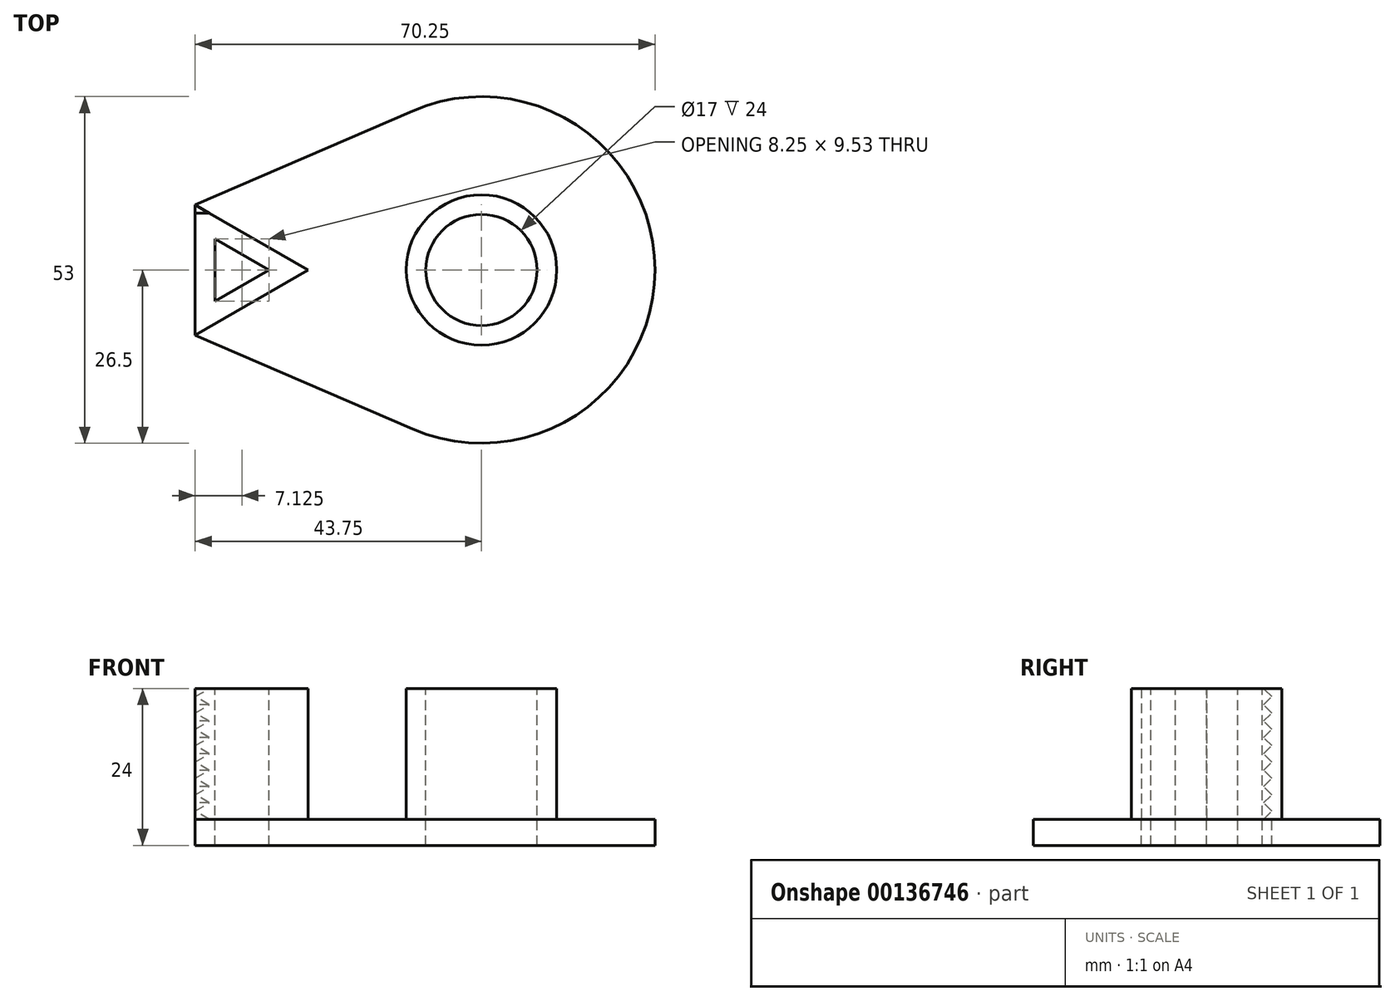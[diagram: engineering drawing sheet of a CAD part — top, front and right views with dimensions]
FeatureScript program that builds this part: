
annotation { "Feature Type Name" : "Feature", "Feature Type Description" : "" }
export const myFeature = defineFeature(function(context is Context, id is Id, definition is map)
    precondition{}
    {
        {
            var Q0;
            Q0=qCreatedBy(makeId("Top.planeOp"),FACE);
            var sketch = newSketch(context, id + "F0", { "sketchPlane" : qUnion([Q0])});
            skCircle(sketch, "E0", {"center": v(0, 0) * mm, "radius": 11.5 * mm});
            skCircle(sketch, "E1.cCircle", {"center": v(-38, 0) * mm, "radius": 11.5 * mm, "construction": true});
            skLineSegment(sketch, "E1.0", {"start": v(-26.5, 0) * mm, "end": v(-43.75, -9.96) * mm});
            skLineSegment(sketch, "E1.1", {"start": v(-43.75, -9.96) * mm, "end": v(-43.75, 9.96) * mm});
            skLineSegment(sketch, "E1.2", {"start": v(-43.75, 9.96) * mm, "end": v(-26.5, 0) * mm});
            skCircle(sketch, "E2", {"center": v(0, 0) * mm, "radius": 26.5 * mm});
            skCircle(sketch, "E3.0", {"center": v(0, 0) * mm, "radius": 8.5 * mm});
            skLineSegment(sketch, "E4.0", {"start": v(-40.75, -4.76) * mm, "end": v(-40.75, 4.76) * mm});
            skLineSegment(sketch, "E4.1", {"start": v(-32.5, 0) * mm, "end": v(-40.75, -4.76) * mm});
            skLineSegment(sketch, "E4.2", {"start": v(-40.75, 4.76) * mm, "end": v(-32.5, 0) * mm});
            skLineSegment(sketch, "E5", {"start": v(-43.75, 9.96) * mm, "end": v(-10.51, 24.32) * mm});
            skLineSegment(sketch, "E6", {"start": v(-43.75, -9.96) * mm, "end": v(-10.51, -24.32) * mm});
            skSolve(sketch);
        }
        {
            var Q0;
            Q0=makeQuery(id+"F0.imprint","IMPRINT",FACE,{"disambiguationData":[TD([[makeQuery(id+"F0.imprint","IMPRINT",EDGE,{"derivedFrom":sQuery(id+"F0.wireOp",EDGE,"E1.0")}),-1.0]])]});
            var Q1;
            {var subQ0=sQuery(id+"F0.wireOp",EDGE,"E1.2");Q1=makeQuery(id+"F0.imprint","IMPRINT",FACE,{"disambiguationData":[TD([[makeQuery(id+"F0.imprint","IMPRINT",EDGE,{"derivedFrom":subQ0}),1.0]])]});}
            var Q2;
            {var subQ3=sQuery(id+"F0.wireOp",EDGE,"z8s4RITF-nqhp-2gdC-14wx-kjl4jssF1Atr");Q2=makeQuery(id+"F0.imprint","IMPRINT",FACE,{"disambiguationData":[TD([[makeQuery(id+"F0.imprint","IMPRINT",EDGE,{"derivedFrom":subQ3}),-1.0]])]});}
            var Q3;
            Q3=makeQuery(id+"F0.imprint","IMPRINT",FACE,{"disambiguationData":[TD([[makeQuery(id+"F0.imprint","IMPRINT",EDGE,{"derivedFrom":sQuery(id+"F0.wireOp",EDGE,"E0")}),-1.0]])]});
            var Q4;
            Q4=makeQuery(id+"F0.imprint","IMPRINT",FACE,{"disambiguationData":[TD([[makeQuery(id+"F0.imprint","IMPRINT",EDGE,{"derivedFrom":sQuery(id+"F0.wireOp",EDGE,"E0")}),1.0]])]});
            var Q5;
            {var subQ3=sQuery(id+"F0.wireOp",EDGE,"0OVe6Yyi-jqsT-2UGS-JQE2-E6pO5a9C04rJ");Q5=makeQuery(id+"F0.imprint","IMPRINT",FACE,{"disambiguationData":[TD([[makeQuery(id+"F0.imprint","IMPRINT",EDGE,{"derivedFrom":subQ3}),-1.0]])]});}
            var Q6;
            {var subQ0=sQuery(id+"F0.wireOp",EDGE,"E1.0");Q6=makeQuery(id+"F0.imprint","IMPRINT",FACE,{"disambiguationData":[TD([[makeQuery(id+"F0.imprint","IMPRINT",EDGE,{"derivedFrom":subQ0}),1.0]])]});}
            extrude(context, id + "F1", {"entities" : qUnion([Q0, Q1, Q2, Q3, Q4, Q5, Q6]), "oppositeDirection" : true, "depth" : 4 * mm, "offsetDistance" : 25 * mm});
        }
        {
            var Q0;
            Q0=makeQuery(id+"F0.imprint","IMPRINT",FACE,{"disambiguationData":[TD([[makeQuery(id+"F0.imprint","IMPRINT",EDGE,{"derivedFrom":sQuery(id+"F0.wireOp",EDGE,"E1.0")}),-1.0]])]});
            var Q1;
            Q1=makeQuery(id+"F0.imprint","IMPRINT",FACE,{"disambiguationData":[TD([[makeQuery(id+"F0.imprint","IMPRINT",EDGE,{"derivedFrom":sQuery(id+"F0.wireOp",EDGE,"E0")}),1.0]])]});
            extrude(context, id + "F2", {"entities" : qUnion([Q0, Q1]), "operationType" : NewBodyOperationType.ADD, "depth" : 20 * mm, "offsetDistance" : 25 * mm});
        }
        {
            var Q0;
            {var subQ0=sQuery(id+"F0.wireOp",EDGE,"E1.1");Q0=makeQuery(id+"F2.boolean.opBoolean","MERGE",FACE,{"derivedFrom":[makeQuery(id+"F1.opExtrude","SWEPT_FACE",FACE,{"disambiguationData":[OSD([subQ0])]}),makeQuery(id+"F2.opExtrude","SWEPT_FACE",FACE,{"disambiguationData":[OSD([subQ0])]})]});}
            var sketch = newSketch(context, id + "F3", { "sketchPlane" : qUnion([Q0])});
            skLineSegment(sketch, "E7", {"start": v(-8.7, 20) * mm, "end": v(-9.96, 18.75) * mm});
            skLineSegment(sketch, "E8", {"start": v(-9.96, 18.75) * mm, "end": v(-8.7, 17.5) * mm});
            skLineSegment(sketch, "E9", {"start": v(-8.7, 20) * mm, "end": v(-8.7, 17.5) * mm});
            skLineSegment(sketch, "E10.0.1.0", {"start": v(-8.7, 17.5) * mm, "end": v(-8.7, 15) * mm});
            skLineSegment(sketch, "E10.0.1.1", {"start": v(-9.96, 16.25) * mm, "end": v(-8.7, 15) * mm});
            skLineSegment(sketch, "E10.0.1.2", {"start": v(-8.7, 17.5) * mm, "end": v(-9.96, 16.25) * mm});
            skLineSegment(sketch, "E10.0.2.0", {"start": v(-8.7, 15) * mm, "end": v(-8.7, 12.5) * mm});
            skLineSegment(sketch, "E10.0.2.1", {"start": v(-9.96, 13.75) * mm, "end": v(-8.7, 12.5) * mm});
            skLineSegment(sketch, "E10.0.2.2", {"start": v(-8.7, 15) * mm, "end": v(-9.96, 13.75) * mm});
            skLineSegment(sketch, "E10.0.3.0", {"start": v(-8.7, 12.5) * mm, "end": v(-8.7, 10) * mm});
            skLineSegment(sketch, "E10.0.3.1", {"start": v(-9.96, 11.25) * mm, "end": v(-8.7, 10) * mm});
            skLineSegment(sketch, "E10.0.3.2", {"start": v(-8.7, 12.5) * mm, "end": v(-9.96, 11.25) * mm});
            skLineSegment(sketch, "E10.0.4.0", {"start": v(-8.7, 10) * mm, "end": v(-8.7, 7.5) * mm});
            skLineSegment(sketch, "E10.0.4.1", {"start": v(-9.96, 8.75) * mm, "end": v(-8.7, 7.5) * mm});
            skLineSegment(sketch, "E10.0.4.2", {"start": v(-8.7, 10) * mm, "end": v(-9.96, 8.75) * mm});
            skLineSegment(sketch, "E10.0.5.0", {"start": v(-8.7, 7.5) * mm, "end": v(-8.7, 5) * mm});
            skLineSegment(sketch, "E10.0.5.1", {"start": v(-9.96, 6.25) * mm, "end": v(-8.7, 5) * mm});
            skLineSegment(sketch, "E10.0.5.2", {"start": v(-8.7, 7.5) * mm, "end": v(-9.96, 6.25) * mm});
            skLineSegment(sketch, "E10.0.6.0", {"start": v(-8.7, 5) * mm, "end": v(-8.7, 2.5) * mm});
            skLineSegment(sketch, "E10.0.6.1", {"start": v(-9.96, 3.75) * mm, "end": v(-8.7, 2.5) * mm});
            skLineSegment(sketch, "E10.0.6.2", {"start": v(-8.7, 5) * mm, "end": v(-9.96, 3.75) * mm});
            skLineSegment(sketch, "E10.0.7.0", {"start": v(-8.7, 2.5) * mm, "end": v(-8.7, 0) * mm});
            skLineSegment(sketch, "E10.0.7.1", {"start": v(-9.96, 1.25) * mm, "end": v(-8.7, 0) * mm});
            skLineSegment(sketch, "E10.0.7.2", {"start": v(-8.7, 2.5) * mm, "end": v(-9.96, 1.25) * mm});
            skLineSegment(sketch, "E10.direction1", {"start": v(-8.7, 17.5) * mm, "end": v(-1.4, 17.5) * mm, "construction": true});
            skLineSegment(sketch, "E10.direction2", {"start": v(-8.7, 17.5) * mm, "end": v(-8.7, 15) * mm, "construction": true});
            skLineSegment(sketch, "E11", {"start": v(-8.7, 0) * mm, "end": v(-9.96, 0) * mm});
            skLineSegment(sketch, "E12", {"start": v(-9.96, 0) * mm, "end": v(-9.96, 1.25) * mm});
            skSolve(sketch);
        }
        {
            var Q0;
            Q0=makeQuery(id+"F3.imprint","IMPRINT",FACE,{"disambiguationData":[TD([[makeQuery(id+"F3.imprint","IMPRINT",EDGE,{"derivedFrom":sQuery(id+"F3.wireOp",EDGE,"E10.0.7.1")}),-1.0]])]});
            var Q1;
            {var subQ0=sQuery(id+"F3.wireOp",EDGE,"E10.0.6.1");Q1=makeQuery(id+"F3.imprint","IMPRINT",FACE,{"disambiguationData":[TD([[makeQuery(id+"F3.imprint","IMPRINT",EDGE,{"derivedFrom":subQ0}),-1.0]])]});}
            var Q2;
            {var subQ0=sQuery(id+"F3.wireOp",EDGE,"E10.0.5.1");Q2=makeQuery(id+"F3.imprint","IMPRINT",FACE,{"disambiguationData":[TD([[makeQuery(id+"F3.imprint","IMPRINT",EDGE,{"derivedFrom":subQ0}),-1.0]])]});}
            var Q3;
            {var subQ0=sQuery(id+"F3.wireOp",EDGE,"E10.0.4.1");Q3=makeQuery(id+"F3.imprint","IMPRINT",FACE,{"disambiguationData":[TD([[makeQuery(id+"F3.imprint","IMPRINT",EDGE,{"derivedFrom":subQ0}),-1.0]])]});}
            var Q4;
            {var subQ0=sQuery(id+"F3.wireOp",EDGE,"E10.0.3.1");Q4=makeQuery(id+"F3.imprint","IMPRINT",FACE,{"disambiguationData":[TD([[makeQuery(id+"F3.imprint","IMPRINT",EDGE,{"derivedFrom":subQ0}),-1.0]])]});}
            var Q5;
            {var subQ0=sQuery(id+"F3.wireOp",EDGE,"E10.0.2.1");Q5=makeQuery(id+"F3.imprint","IMPRINT",FACE,{"disambiguationData":[TD([[makeQuery(id+"F3.imprint","IMPRINT",EDGE,{"derivedFrom":subQ0}),-1.0]])]});}
            var Q6;
            {var subQ0=sQuery(id+"F3.wireOp",EDGE,"E10.0.1.1");Q6=makeQuery(id+"F3.imprint","IMPRINT",FACE,{"disambiguationData":[TD([[makeQuery(id+"F3.imprint","IMPRINT",EDGE,{"derivedFrom":subQ0}),-1.0]])]});}
            var Q7;
            {var subQ0=sQuery(id+"F3.wireOp",EDGE,"E8");Q7=makeQuery(id+"F3.imprint","IMPRINT",FACE,{"disambiguationData":[TD([[makeQuery(id+"F3.imprint","IMPRINT",EDGE,{"derivedFrom":subQ0}),-1.0]])]});}
            var Q8;
            {var subQ0=sQuery(id+"F3.wireOp",EDGE,"E7");Q8=makeQuery(id+"F3.imprint","IMPRINT",FACE,{"disambiguationData":[TD([[makeQuery(id+"F3.imprint","IMPRINT",EDGE,{"derivedFrom":subQ0}),-1.0]])]});}
            extrude(context, id + "F4", {"entities" : qUnion([Q0, Q1, Q2, Q3, Q4, Q5, Q6, Q7, Q8]), "operationType" : NewBodyOperationType.REMOVE, "oppositeDirection" : true, "depth" : 10 * mm, "offsetDistance" : 25 * mm});
        }
    });
